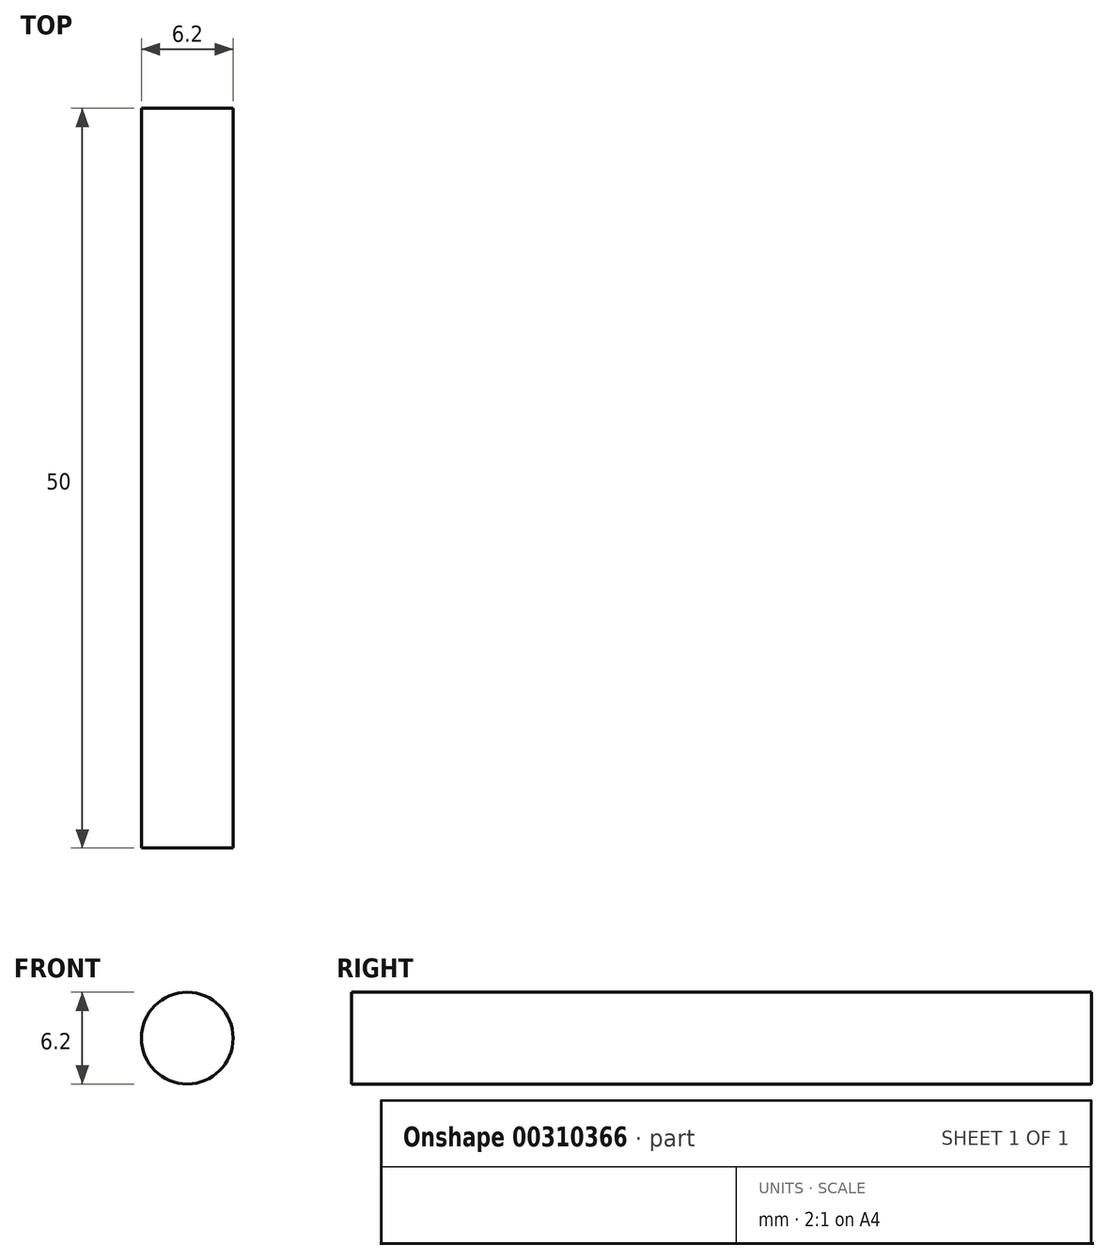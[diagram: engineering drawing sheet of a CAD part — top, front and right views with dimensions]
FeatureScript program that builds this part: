
annotation { "Feature Type Name" : "Feature", "Feature Type Description" : "" }
export const myFeature = defineFeature(function(context is Context, id is Id, definition is map)
    precondition{}
    {
        {
            var Q0;
            Q0=qCreatedBy(makeId("Front.planeOp"),FACE);
            var sketch = newSketch(context, id + "F0", { "sketchPlane" : qUnion([Q0])});
            skCircle(sketch, "E0", {"center": v(0, 0) * mm, "radius": 3.1 * mm});
            skSolve(sketch);
        }
        {
            var Q0;
            Q0 = qSketchRegion(id + "F0", true);
            extrude(context, id + "F1", {"entities" : qUnion([Q0]), "depth" : 50 * mm});
        }
    });
